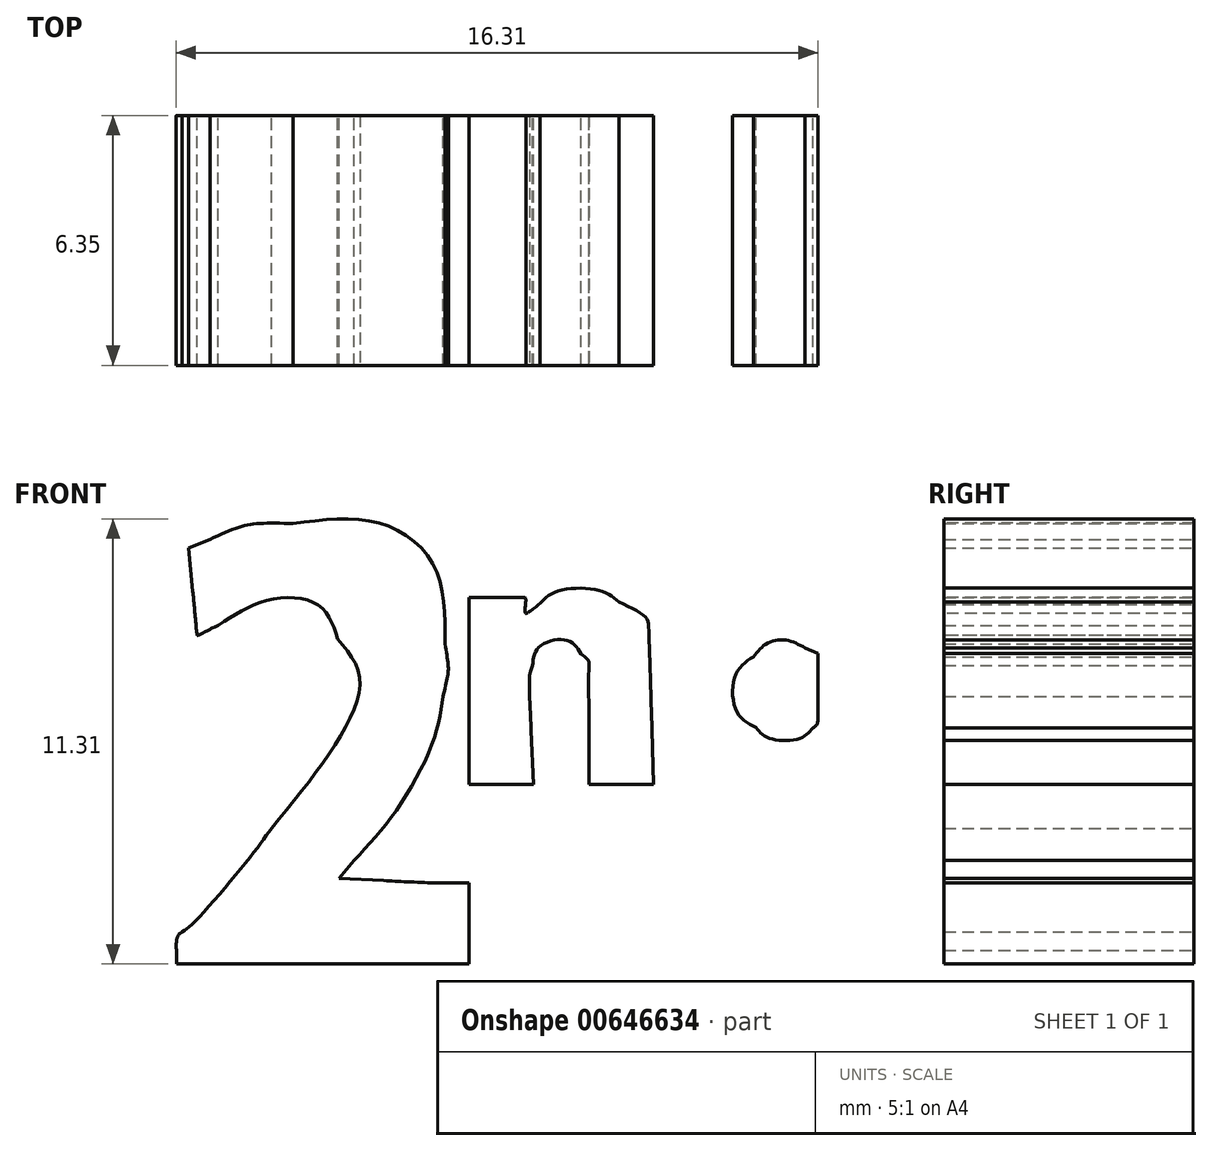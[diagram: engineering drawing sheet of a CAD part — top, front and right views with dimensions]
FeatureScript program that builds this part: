
annotation { "Feature Type Name" : "Feature", "Feature Type Description" : "" }
export const myFeature = defineFeature(function(context is Context, id is Id, definition is map)
    precondition{}
    {
        {
            var Q0;
            Q0=qCreatedBy(makeId("Front.planeOp"),FACE);
            var sketch = newSketch(context, id + "F0", { "sketchPlane" : qUnion([Q0])});
            skFitSpline(sketch, "E0", {"points": [v(-8.91, -5.7) * mm, v(-8.91, -5.49) * mm, v(-8.86, -5.3) * mm, v(-8.76, -5.23) * mm]});
            skFitSpline(sketch, "E1", {"points": [v(-8.76, -5.23) * mm, v(-8.46, -4.98) * mm, v(-7.1, -3.4) * mm, v(-6.5, -2.6) * mm]});
            skFitSpline(sketch, "E2", {"points": [v(-6.5, -2.6) * mm, v(-4.8, -0.35) * mm, v(-4.26, 1.22) * mm, v(-4.81, 2.21) * mm]});
            skFitSpline(sketch, "E3", {"points": [v(-4.81, 2.21) * mm, v(-5.3, 3.06) * mm, v(-6.56, 3.2) * mm, v(-7.85, 2.56) * mm]});
            skFitSpline(sketch, "E4", {"points": [v(-7.85, 2.56) * mm, v(-8.14, 2.41) * mm, v(-8.38, 2.3) * mm, v(-8.38, 2.31) * mm]});
            skFitSpline(sketch, "E5", {"points": [v(-8.38, 2.31) * mm, v(-8.39, 2.32) * mm, v(-8.44, 2.82) * mm, v(-8.5, 3.42) * mm]});
            skFitSpline(sketch, "E6", {"points": [v(-8.06, 4.74) * mm, v(-7.32, 5.05) * mm, v(-6.84, 5.14) * mm, v(-5.95, 5.14) * mm]});
            skFitSpline(sketch, "E7", {"points": [v(-5.95, 5.14) * mm, v(-3.75, 5.15) * mm, v(-2.36, 4.05) * mm, v(-2.09, 2.08) * mm]});
            skFitSpline(sketch, "E8", {"points": [v(-2.09, 2.08) * mm, v(-2, 1.53) * mm, v(-2.02, 1.3) * mm, v(-2.14, 0.75) * mm]});
            skFitSpline(sketch, "E9", {"points": [v(-2.14, 0.75) * mm, v(-2.4, -0.42) * mm, v(-3.37, -2.2) * mm, v(-4.4, -3.42) * mm]});
            skLineSegment(sketch, "E10", {"start": v(-8.5, 3.42) * mm, "end": v(-8.6, 4.52) * mm});
            skLineSegment(sketch, "E11", {"start": v(-8.6, 4.52) * mm, "end": v(-8.06, 4.74) * mm});
            skFitSpline(sketch, "E12", {"points": [v(-3.65, -3.93) * mm, v(-3.02, -3.96) * mm, v(-2.28, -3.99) * mm, v(-2, -3.99) * mm]});
            skLineSegment(sketch, "E13", {"start": v(-4.4, -3.42) * mm, "end": v(-4.78, -3.87) * mm});
            skLineSegment(sketch, "E14", {"start": v(-4.78, -3.87) * mm, "end": v(-3.65, -3.93) * mm});
            skFitSpline(sketch, "E15", {"points": [v(5.25, -1.3) * mm, v(4.81, -1.08) * mm, v(4.62, -0.91) * mm, v(4.38, -0.55) * mm]});
            skFitSpline(sketch, "E16", {"points": [v(4.38, -0.55) * mm, v(3.52, 0.75) * mm, v(4.02, 2.59) * mm, v(5.4, 3.2) * mm]});
            skFitSpline(sketch, "E17", {"points": [v(5.4, 3.2) * mm, v(5.82, 3.38) * mm, v(6.72, 3.45) * mm, v(7.14, 3.33) * mm]});
            skLineSegment(sketch, "E18", {"start": v(-2, -3.99) * mm, "end": v(-1.48, -3.99) * mm});
            skLineSegment(sketch, "E19", {"start": v(-1.48, -3.99) * mm, "end": v(-1.48, -5.02) * mm});
            skLineSegment(sketch, "E20", {"start": v(-1.48, -5.02) * mm, "end": v(-1.48, -6.05) * mm});
            skLineSegment(sketch, "E21", {"start": v(-1.48, -6.05) * mm, "end": v(-5.2, -6.05) * mm});
            skLineSegment(sketch, "E22", {"start": v(-5.2, -6.05) * mm, "end": v(-8.91, -6.05) * mm});
            skLineSegment(sketch, "E23", {"start": v(-8.91, -6.05) * mm, "end": v(-8.91, -5.7) * mm});
            skLineSegment(sketch, "E24", {"start": v(-8.91, -5.7) * mm, "end": v(-8.91, -5.7) * mm});
            skFitSpline(sketch, "E25", {"points": [v(8.29, -1.48) * mm, v(7.79, -1.48) * mm, v(7.66, -1.45) * mm, v(7.66, -1.35) * mm]});
            skFitSpline(sketch, "E26", {"points": [v(7.66, -1.35) * mm, v(7.66, -1.18) * mm, v(7.67, -1.18) * mm, v(7.25, -1.4) * mm]});
            skFitSpline(sketch, "E27", {"points": [v(7.25, -1.4) * mm, v(6.7, -1.68) * mm, v(5.94, -1.64) * mm, v(5.25, -1.3) * mm]});
            skLineSegment(sketch, "E28", {"start": v(7.14, 3.33) * mm, "end": v(7.39, 3.26) * mm});
            skLineSegment(sketch, "E29", {"start": v(7.39, 3.26) * mm, "end": v(7.39, 4.66) * mm});
            skLineSegment(sketch, "E30", {"start": v(7.39, 4.66) * mm, "end": v(7.39, 6.05) * mm});
            skLineSegment(sketch, "E31", {"start": v(7.39, 6.05) * mm, "end": v(8.13, 6.02) * mm});
            skLineSegment(sketch, "E32", {"start": v(8.13, 6.02) * mm, "end": v(8.87, 6) * mm});
            skLineSegment(sketch, "E33", {"start": v(8.87, 6) * mm, "end": v(8.9, 2.26) * mm});
            skLineSegment(sketch, "E34", {"start": v(8.9, 2.26) * mm, "end": v(8.91, -1.48) * mm});
            skLineSegment(sketch, "E35", {"start": v(8.91, -1.48) * mm, "end": v(8.29, -1.48) * mm});
            skFitSpline(sketch, "E36", {"points": [v(7.26, -0.05) * mm, v(7.36, 0.04) * mm, v(7.39, 0.28) * mm, v(7.39, 0.95) * mm]});
            skFitSpline(sketch, "E37", {"points": [v(7.06, 1.98) * mm, v(6.59, 2.18) * mm, v(6.08, 2.1) * mm, v(5.75, 1.76) * mm]});
            skFitSpline(sketch, "E38", {"points": [v(5.75, 1.76) * mm, v(5.3, 1.3) * mm, v(5.33, 0.36) * mm, v(5.82, -0.04) * mm]});
            skFitSpline(sketch, "E39", {"points": [v(5.82, -0.04) * mm, v(6.13, -0.3) * mm, v(6.94, -0.3) * mm, v(7.26, -0.05) * mm]});
            skLineSegment(sketch, "E40", {"start": v(7.39, 0.95) * mm, "end": v(7.39, 1.84) * mm});
            skLineSegment(sketch, "E41", {"start": v(7.39, 1.84) * mm, "end": v(7.06, 1.98) * mm});
            skLineSegment(sketch, "E42", {"start": v(7.26, -0.05) * mm, "end": v(7.26, -0.05) * mm});
            skFitSpline(sketch, "E43", {"points": [v(-0.76, 3.27) * mm, v(-0.1, 3.27) * mm, v(-0.05, 3.25) * mm, v(-0.05, 3.09) * mm]});
            skFitSpline(sketch, "E44", {"points": [v(-0.05, 3.09) * mm, v(-0.05, 2.86) * mm, v(-0.01, 2.86) * mm, v(0.32, 3.1) * mm]});
            skFitSpline(sketch, "E45", {"points": [v(0.32, 3.1) * mm, v(0.74, 3.42) * mm, v(1.83, 3.44) * mm, v(2.33, 3.15) * mm]});
            skFitSpline(sketch, "E46", {"points": [v(2.33, 3.15) * mm, v(3, 2.77) * mm, v(3.08, 2.48) * mm, v(3.15, 0.36) * mm]});
            skLineSegment(sketch, "E47", {"start": v(-1.48, 0.9) * mm, "end": v(-1.48, 3.27) * mm});
            skLineSegment(sketch, "E48", {"start": v(-1.48, 3.27) * mm, "end": v(-0.76, 3.27) * mm});
            skFitSpline(sketch, "E49", {"points": [v(1.57, 0.08) * mm, v(1.57, 1.58) * mm, v(1.56, 1.65) * mm, v(1.37, 1.83) * mm]});
            skFitSpline(sketch, "E50", {"points": [v(1.37, 1.83) * mm, v(1, 2.17) * mm, v(0.3, 2) * mm, v(0.14, 1.53) * mm]});
            skFitSpline(sketch, "E51", {"points": [v(0.14, 1.53) * mm, v(0.07, 1.35) * mm, v(0.06, 0.79) * mm, v(0.1, -0.11) * mm]});
            skLineSegment(sketch, "E52", {"start": v(3.15, 0.36) * mm, "end": v(3.2, -1.48) * mm});
            skLineSegment(sketch, "E53", {"start": v(3.2, -1.48) * mm, "end": v(2.39, -1.48) * mm});
            skLineSegment(sketch, "E54", {"start": v(2.39, -1.48) * mm, "end": v(1.57, -1.48) * mm});
            skLineSegment(sketch, "E55", {"start": v(1.57, -1.48) * mm, "end": v(1.57, 0.08) * mm});
            skLineSegment(sketch, "E56", {"start": v(0.1, -0.11) * mm, "end": v(0.16, -1.48) * mm});
            skLineSegment(sketch, "E57", {"start": v(0.16, -1.48) * mm, "end": v(-0.66, -1.48) * mm});
            skLineSegment(sketch, "E58", {"start": v(-0.66, -1.48) * mm, "end": v(-1.48, -1.48) * mm});
            skLineSegment(sketch, "E59", {"start": v(-1.48, -1.48) * mm, "end": v(-1.48, 0.9) * mm});
            skSolve(sketch);
        }
        {
            var Q0;
            Q0 = qSketchRegion(id + "F0", true);
            extrude(context, id + "F1", {"entities" : qUnion([Q0]), "depth" : 6.35 * mm, "offsetDistance" : 25.4 * mm});
        }
    });
